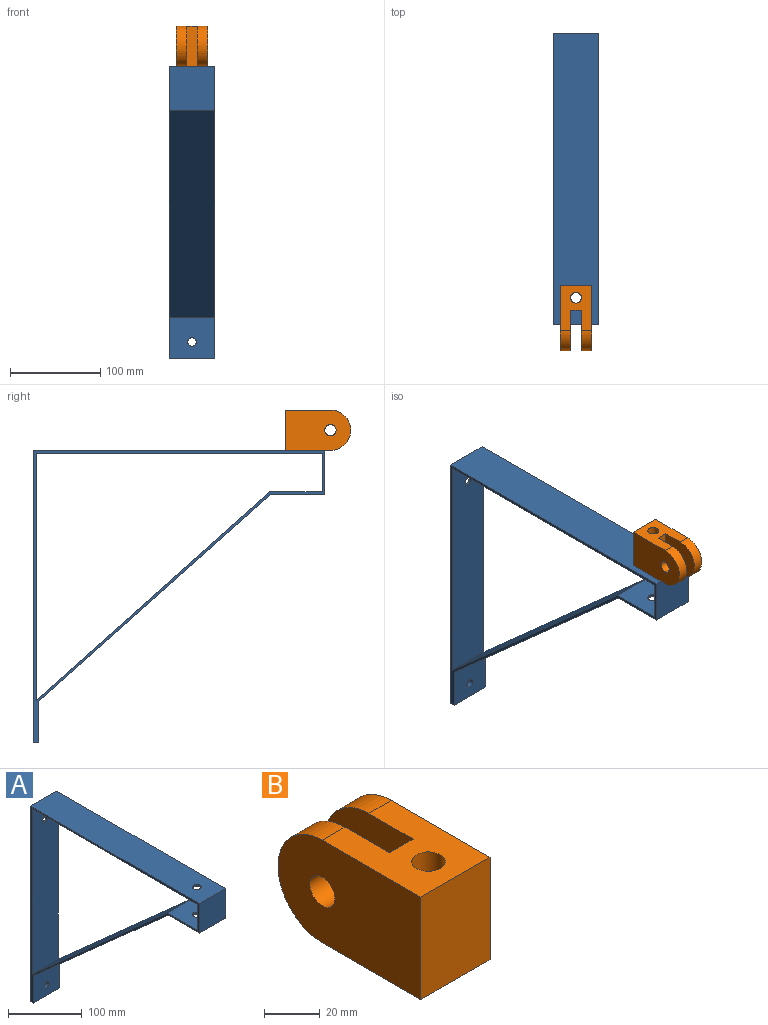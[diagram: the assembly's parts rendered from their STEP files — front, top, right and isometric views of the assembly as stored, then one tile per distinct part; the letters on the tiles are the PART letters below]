
ASSEMBLY  parts=2 mates=1
PART A: 18 faces, bbox 50x323.9x323.9 mm
  f0: plane 323.85x50mm, normal (0,1,0), area 16050mm2, adj f1,f11,f12,f13,f16,f17
  f1: plane 323.85x50mm, normal (0,0,1), area 16079.4mm2, adj f0,f2,f12,f13,f14
  f2: plane 50x49mm, normal (0,-1,0), area 2450mm2, adj f1,f3,f12,f13
  f3: plane 60x50mm, normal (0,0,-1), area 2886.9mm2, adj f2,f4,f12,f13,f15
  f4: plane 257.85x229.85mm, normal (0,-0.67,-0.75), area 17271.2mm2, adj f3,f5,f12,f13
  f5: plane 50x45mm, normal (0,-1,0), area 2178.7mm2, adj f4,f11,f12,f13,f17
  f6: plane 274.51x50mm, normal (0,-1,0), area 13654mm2, adj f7,f10,f12,f13,f16
  f7: plane 259.71x231.51mm, normal (0,0.67,0.75), area 17395.6mm2, adj f6,f8,f12,f13
  f8: plane 58.14x50mm, normal (0,0,1), area 2794.1mm2, adj f7,f9,f12,f13,f15
  f9: plane 50x43mm, normal (0,1,0), area 2150mm2, adj f8,f10,f12,f13
  f10: plane 317.85x50mm, normal (0,0,-1), area 15779.4mm2, adj f6,f9,f12,f13,f14
  f11: plane 50x6mm, normal (0,0,-1), area 300mm2, adj f0,f5,f12,f13
  f12: plane 323.85x323.85mm, normal (1,0,0), area 3421.8mm2, adj f0,f1,f2,f3,f4,f5,f6,f7
  f13: plane 323.85x323.85mm, normal (-1,0,0), area 3421.8mm2, adj f0,f1,f2,f3,f4,f5,f6,f7
  f14: cylinder r=6mm len=12mm, axis (0,0,-1), area 113.1mm2, adj f1,f10
  f15: cylinder r=6mm len=12mm, axis (0,0,-1), area 113.1mm2, adj f3,f8
  f16: cylinder r=4.76mm len=9.53mm, axis (0,1,0), area 89.8mm2, adj f0,f6
  f17: cylinder r=4.76mm len=9.53mm, axis (0,1,0), area 179.5mm2, adj f0,f5
PART B: 13 faces, bbox 35x72.5x45 mm
  f0: cylinder r=22.5mm len=45mm, axis (-1,0,0), area 812.9mm2, adj f2,f4,f7,f10
  f1: cylinder r=6.35mm len=12.7mm, axis (-1,0,0), area 458.8mm2, adj f7,f10
  f2: plane 50x35mm, normal (0,0,-1), area 1366.9mm2, adj f0,f3,f6,f7,f8,f9,f10,f11
  f3: cylinder r=22.5mm len=45mm, axis (-1,0,0), area 812.9mm2, adj f2,f4,f8,f9
  f4: plane 50x35mm, normal (0,0,1), area 1366.9mm2, adj f0,f3,f6,f7,f8,f9,f10,f11
  f5: cylinder r=6.35mm len=12.7mm, axis (-1,0,0), area 458.8mm2, adj f8,f9
  f6: plane 45x35mm, normal (0,-1,0), area 1575mm2, adj f2,f4,f7,f8
  f7: plane 72.5x45mm, normal (1,0,0), area 2918.5mm2, adj f0,f1,f2,f4,f6
  f8: plane 72.5x45mm, normal (-1,0,0), area 2918.5mm2, adj f2,f3,f4,f5,f6
  f9: plane 45x45mm, normal (1,0,0), area 1681mm2, adj f2,f3,f4,f5,f11
  f10: plane 45x45mm, normal (-1,0,0), area 1681mm2, adj f0,f1,f2,f4,f11
  f11: plane 45x12mm, normal (0,1,0), area 540mm2, adj f2,f4,f9,f10
  f12: cylinder r=6mm len=45mm, axis (0,0,1), area 1696.5mm2, adj f2,f4
PLACE A at identity
PLACE B rot(axis=(-1,0,0),180deg) t=(0,-158.95,169.08)mm
MATE cylindrical B.f12 <-> A.f14  axis (0,0,-1) through (0,-122.7,146.58)mm
